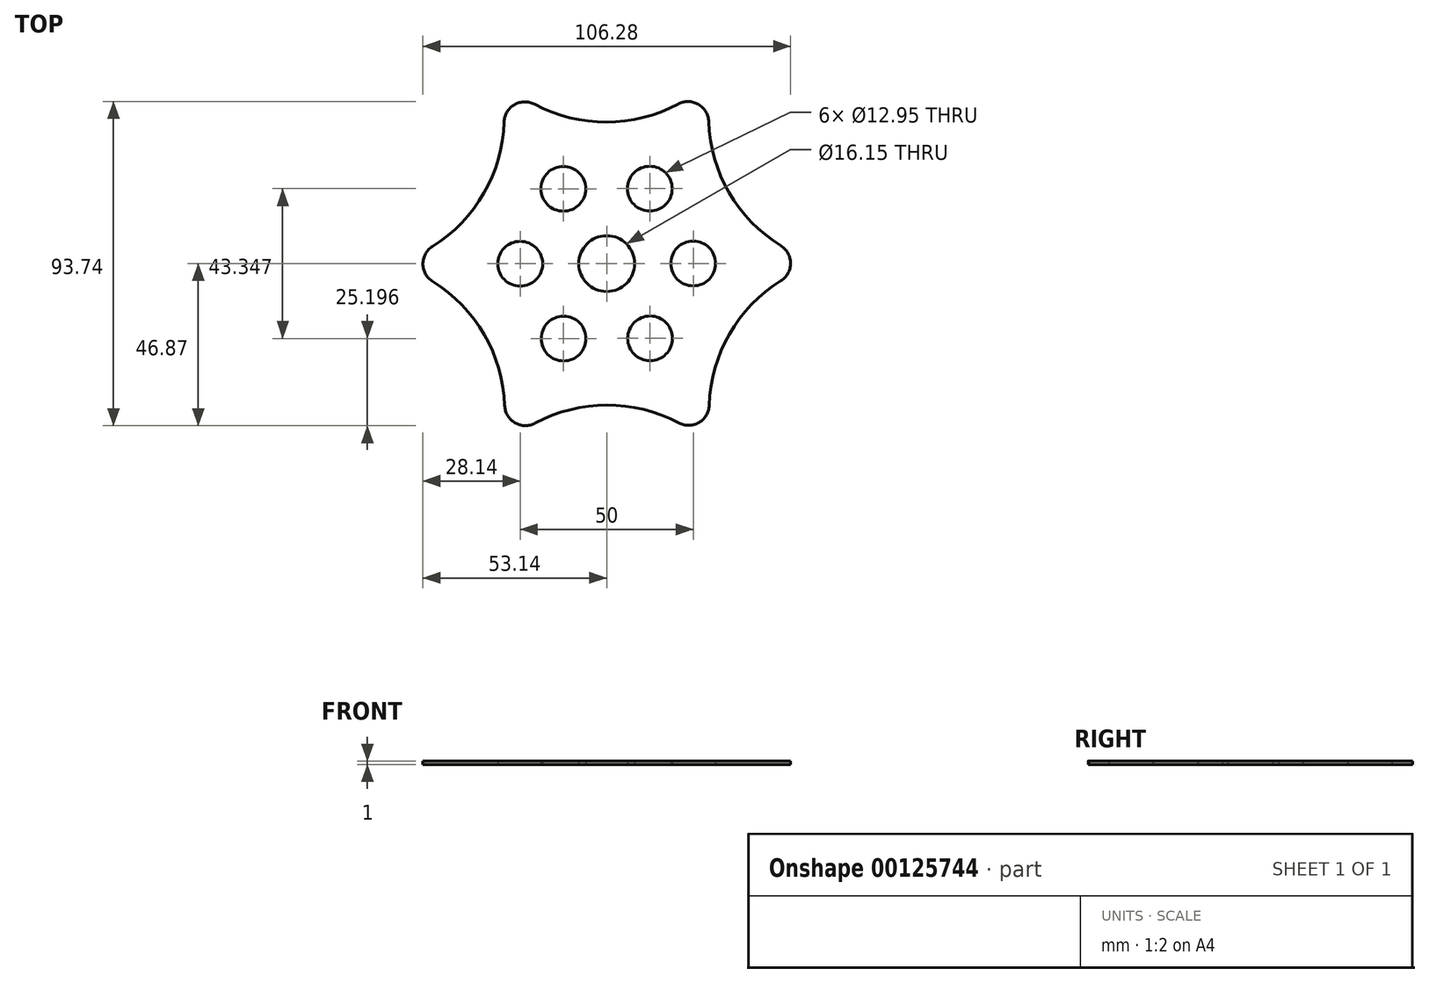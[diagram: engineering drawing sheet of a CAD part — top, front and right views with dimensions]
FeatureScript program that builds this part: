
annotation { "Feature Type Name" : "Feature", "Feature Type Description" : "" }
export const myFeature = defineFeature(function(context is Context, id is Id, definition is map)
    precondition{}
    {
        {
            var Q0;
            Q0=qCreatedBy(makeId("Top.planeOp"),FACE);
            var sketch = newSketch(context, id + "F0", { "sketchPlane" : qUnion([Q0])});
            skCircle(sketch, "E0.cCircle", {"center": v(0, 0) * mm, "radius": 53.7 * mm, "construction": true});
            skLineSegment(sketch, "E0.0", {"start": v(30.9, 53.75) * mm, "end": v(62, 0.11) * mm});
            skLineSegment(sketch, "E0.1", {"start": v(62, 0.11) * mm, "end": v(31.1, -53.64) * mm});
            skLineSegment(sketch, "E0.2", {"start": v(31.1, -53.64) * mm, "end": v(-30.9, -53.75) * mm});
            skLineSegment(sketch, "E0.3", {"start": v(-30.9, -53.75) * mm, "end": v(-62, -0.11) * mm});
            skLineSegment(sketch, "E0.4", {"start": v(-62, -0.11) * mm, "end": v(-31.1, 53.64) * mm});
            skLineSegment(sketch, "E0.5", {"start": v(-31.1, 53.64) * mm, "end": v(30.9, 53.75) * mm});
            skPoint(sketch, "E0.0.midPoint", {"position": v(46.45, 26.93) * mm});
            skArc(sketch, "E1", {"start": v(-20.83, 46.08) * mm, "mid": v(-0.08, 40.92) * mm, "end": v(20.66, 46.15) * mm});
            skArc(sketch, "E2", {"start": v(29.49, 41.07) * mm, "mid": v(35.4, 20.52) * mm, "end": v(50.3, 5.19) * mm});
            skArc(sketch, "E3", {"start": v(50.31, -5) * mm, "mid": v(35.47, -20.4) * mm, "end": v(29.64, -40.96) * mm});
            skArc(sketch, "E4", {"start": v(20.83, -46.08) * mm, "mid": v(0.08, -40.92) * mm, "end": v(-20.66, -46.15) * mm});
            skArc(sketch, "E5", {"start": v(-29.49, -41.07) * mm, "mid": v(-35.4, -20.52) * mm, "end": v(-50.3, -5.19) * mm});
            skArc(sketch, "E6", {"start": v(-50.31, 5) * mm, "mid": v(-35.47, 20.4) * mm, "end": v(-29.64, 40.96) * mm});
            skPoint(sketch, "E7.visualSharp", {"position": v(-31.1, 53.64) * mm});
            skArc(sketch, "E7.filletArc", {"start": v(-20.83, 46.08) * mm, "mid": v(-26.65, 45.97) * mm, "end": v(-29.64, 40.96) * mm});
            skPoint(sketch, "E8.visualSharp", {"position": v(30.9, 53.75) * mm});
            skArc(sketch, "E8.filletArc", {"start": v(29.49, 41.07) * mm, "mid": v(26.48, 46.07) * mm, "end": v(20.66, 46.15) * mm});
            skPoint(sketch, "E9.visualSharp", {"position": v(62, 0.11) * mm});
            skArc(sketch, "E9.filletArc", {"start": v(50.31, -5) * mm, "mid": v(53.14, 0.1) * mm, "end": v(50.3, 5.19) * mm});
            skPoint(sketch, "E10.visualSharp", {"position": v(31.1, -53.64) * mm});
            skArc(sketch, "E10.filletArc", {"start": v(20.83, -46.08) * mm, "mid": v(26.65, -45.97) * mm, "end": v(29.64, -40.96) * mm});
            skPoint(sketch, "E11.visualSharp", {"position": v(-30.9, -53.75) * mm});
            skArc(sketch, "E11.filletArc", {"start": v(-29.49, -41.07) * mm, "mid": v(-26.48, -46.07) * mm, "end": v(-20.66, -46.15) * mm});
            skPoint(sketch, "E12.visualSharp", {"position": v(-62, -0.11) * mm});
            skArc(sketch, "E12.filletArc", {"start": v(-50.31, 5) * mm, "mid": v(-53.14, -0.1) * mm, "end": v(-50.3, -5.19) * mm});
            skCircle(sketch, "E13", {"center": v(-12.54, 21.63) * mm, "radius": 6.47 * mm});
            skCircle(sketch, "E14", {"center": v(12.46, 21.67) * mm, "radius": 6.47 * mm});
            skCircle(sketch, "E15", {"center": v(25, 0.05) * mm, "radius": 6.47 * mm});
            skCircle(sketch, "E16", {"center": v(12.54, -21.63) * mm, "radius": 6.47 * mm});
            skCircle(sketch, "E17", {"center": v(-12.46, -21.67) * mm, "radius": 6.47 * mm});
            skCircle(sketch, "E18", {"center": v(-25, -0.05) * mm, "radius": 6.47 * mm});
            skCircle(sketch, "E19", {"center": v(0, 0) * mm, "radius": 8.07 * mm});
            skSolve(sketch);
        }
        {
            var Q0;
            Q0=makeQuery(id+"F0.imprint","IMPRINT",FACE,{"disambiguationData":[TD([[makeQuery(id+"F0.imprint","IMPRINT",EDGE,{"derivedFrom":sQuery(id+"F0.wireOp",EDGE,"E1")}),-1.0]])]});
            extrude(context, id + "F1", {"entities" : qUnion([Q0]), "depth" : 1 * mm});
        }
    });
